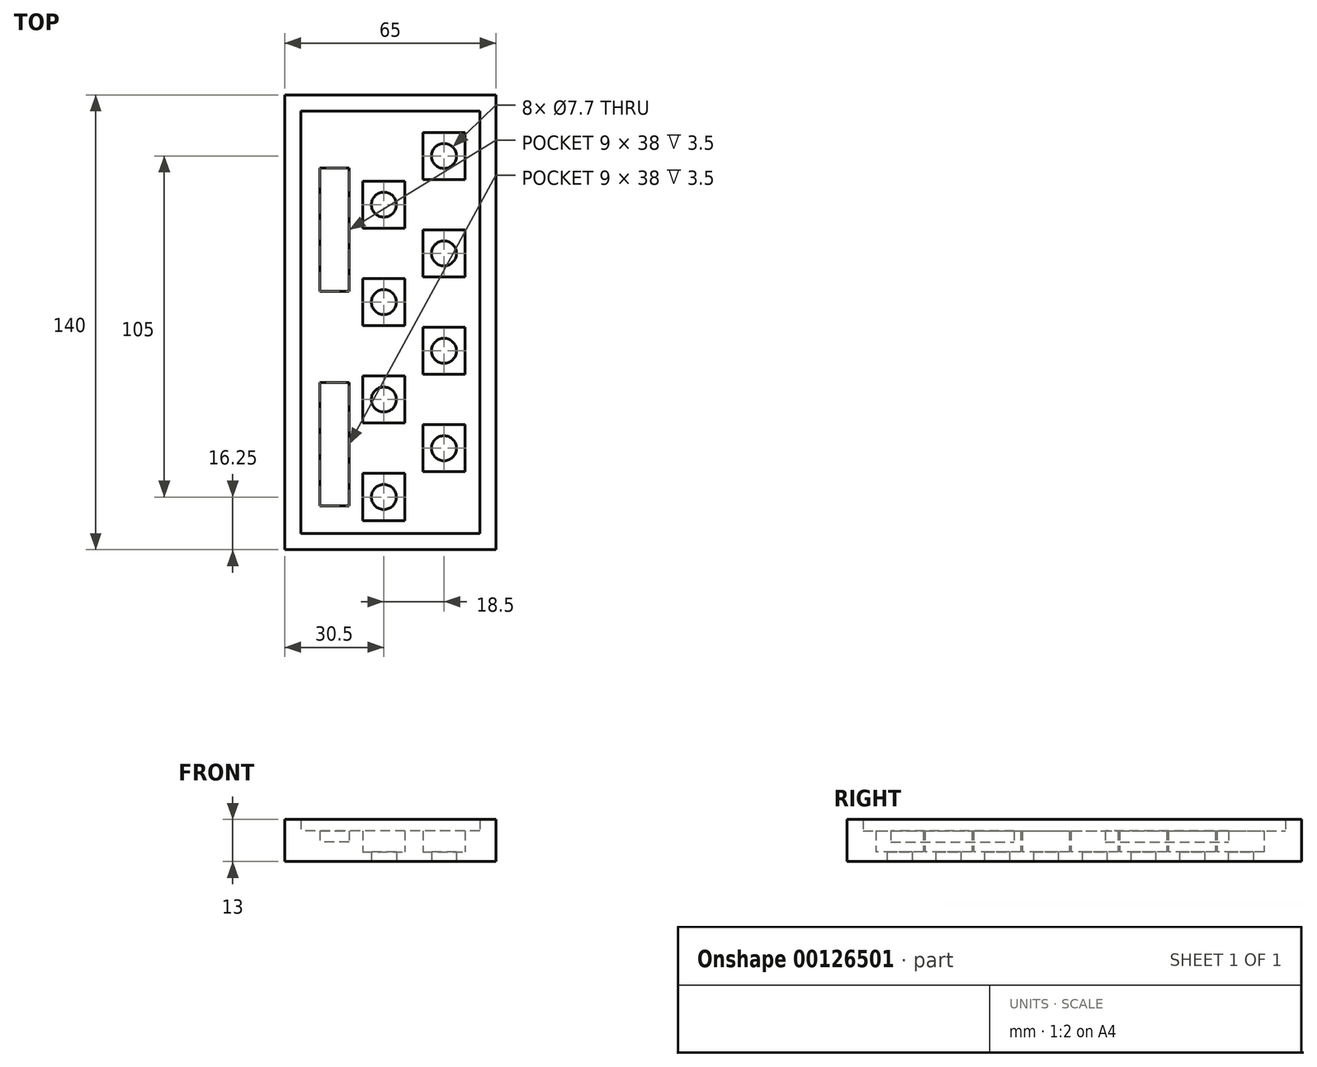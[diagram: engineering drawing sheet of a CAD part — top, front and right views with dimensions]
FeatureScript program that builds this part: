
annotation { "Feature Type Name" : "Feature", "Feature Type Description" : "" }
export const myFeature = defineFeature(function(context is Context, id is Id, definition is map)
    precondition{}
    {
        {
            var Q0;
            Q0=qCreatedBy(makeId("Top.planeOp"),FACE);
            var sketch = newSketch(context, id + "F0", { "sketchPlane" : qUnion([Q0])});
            skLineSegment(sketch, "E0.bottom", {"start": v(-63.75, 69.94) * mm, "end": v(1.25, 69.94) * mm});
            skLineSegment(sketch, "E0.top", {"start": v(-63.75, -70.06) * mm, "end": v(1.25, -70.06) * mm});
            skLineSegment(sketch, "E0.left", {"start": v(-63.75, 69.94) * mm, "end": v(-63.75, -70.06) * mm});
            skLineSegment(sketch, "E0.right", {"start": v(1.25, 69.94) * mm, "end": v(1.25, -70.06) * mm});
            skLineSegment(sketch, "E1.bottom", {"start": v(-8.25, 43.94) * mm, "end": v(-21.25, 43.94) * mm});
            skLineSegment(sketch, "E1.top", {"start": v(-8.25, 58.44) * mm, "end": v(-21.25, 58.44) * mm});
            skLineSegment(sketch, "E1.left", {"start": v(-8.25, 43.94) * mm, "end": v(-8.25, 58.44) * mm});
            skLineSegment(sketch, "E1.right", {"start": v(-21.25, 43.94) * mm, "end": v(-21.25, 58.44) * mm});
            skPoint(sketch, "E1.middle", {"position": v(-14.75, 51.2) * mm});
            skLineSegment(sketch, "E2.bottom", {"start": v(-26.75, 28.94) * mm, "end": v(-39.75, 28.94) * mm});
            skLineSegment(sketch, "E2.top", {"start": v(-26.75, 43.44) * mm, "end": v(-39.75, 43.44) * mm});
            skLineSegment(sketch, "E2.left", {"start": v(-26.75, 28.94) * mm, "end": v(-26.75, 43.44) * mm});
            skLineSegment(sketch, "E2.right", {"start": v(-39.75, 28.94) * mm, "end": v(-39.75, 43.44) * mm});
            skPoint(sketch, "E2.middle", {"position": v(-33.25, 36.2) * mm});
            skLineSegment(sketch, "E3.bottom", {"start": v(-8.25, 13.94) * mm, "end": v(-21.25, 13.94) * mm});
            skLineSegment(sketch, "E3.top", {"start": v(-8.25, 28.44) * mm, "end": v(-21.25, 28.44) * mm});
            skLineSegment(sketch, "E3.left", {"start": v(-8.25, 13.94) * mm, "end": v(-8.25, 28.44) * mm});
            skLineSegment(sketch, "E3.right", {"start": v(-21.25, 13.94) * mm, "end": v(-21.25, 28.44) * mm});
            skPoint(sketch, "E3.middle", {"position": v(-14.75, 21.2) * mm});
            skLineSegment(sketch, "E4.bottom", {"start": v(-26.75, -1.06) * mm, "end": v(-39.75, -1.06) * mm});
            skLineSegment(sketch, "E4.top", {"start": v(-26.75, 13.44) * mm, "end": v(-39.75, 13.44) * mm});
            skLineSegment(sketch, "E4.left", {"start": v(-26.75, -1.06) * mm, "end": v(-26.75, 13.44) * mm});
            skLineSegment(sketch, "E4.right", {"start": v(-39.75, -1.06) * mm, "end": v(-39.75, 13.44) * mm});
            skPoint(sketch, "E4.middle", {"position": v(-33.25, 6.2) * mm});
            skLineSegment(sketch, "E5.bottom", {"start": v(-8.25, -16.06) * mm, "end": v(-21.25, -16.06) * mm});
            skLineSegment(sketch, "E5.top", {"start": v(-8.25, -1.56) * mm, "end": v(-21.25, -1.56) * mm});
            skLineSegment(sketch, "E5.left", {"start": v(-8.25, -16.06) * mm, "end": v(-8.25, -1.56) * mm});
            skLineSegment(sketch, "E5.right", {"start": v(-21.25, -16.06) * mm, "end": v(-21.25, -1.56) * mm});
            skPoint(sketch, "E5.middle", {"position": v(-14.75, -8.8) * mm});
            skLineSegment(sketch, "E6.bottom", {"start": v(-26.75, -31.06) * mm, "end": v(-39.75, -31.06) * mm});
            skLineSegment(sketch, "E6.top", {"start": v(-26.75, -16.56) * mm, "end": v(-39.75, -16.56) * mm});
            skLineSegment(sketch, "E6.left", {"start": v(-26.75, -31.06) * mm, "end": v(-26.75, -16.56) * mm});
            skLineSegment(sketch, "E6.right", {"start": v(-39.75, -31.06) * mm, "end": v(-39.75, -16.56) * mm});
            skPoint(sketch, "E6.middle", {"position": v(-33.25, -23.8) * mm});
            skLineSegment(sketch, "E7.bottom", {"start": v(-8.25, -46.06) * mm, "end": v(-21.25, -46.06) * mm});
            skLineSegment(sketch, "E7.top", {"start": v(-8.25, -31.56) * mm, "end": v(-21.25, -31.56) * mm});
            skLineSegment(sketch, "E7.left", {"start": v(-8.25, -46.06) * mm, "end": v(-8.25, -31.56) * mm});
            skLineSegment(sketch, "E7.right", {"start": v(-21.25, -46.06) * mm, "end": v(-21.25, -31.56) * mm});
            skPoint(sketch, "E7.middle", {"position": v(-14.75, -38.8) * mm});
            skLineSegment(sketch, "E8.bottom", {"start": v(-26.75, -61.06) * mm, "end": v(-39.75, -61.06) * mm});
            skLineSegment(sketch, "E8.top", {"start": v(-26.75, -46.56) * mm, "end": v(-39.75, -46.56) * mm});
            skLineSegment(sketch, "E8.left", {"start": v(-26.75, -61.06) * mm, "end": v(-26.75, -46.56) * mm});
            skLineSegment(sketch, "E8.right", {"start": v(-39.75, -61.06) * mm, "end": v(-39.75, -46.56) * mm});
            skPoint(sketch, "E8.middle", {"position": v(-33.25, -53.8) * mm});
            skCircle(sketch, "E9", {"center": v(-14.75, 51.2) * mm, "radius": 3.85 * mm});
            skCircle(sketch, "E10", {"center": v(-33.25, 36.2) * mm, "radius": 3.85 * mm});
            skCircle(sketch, "E11", {"center": v(-14.75, 21.2) * mm, "radius": 3.85 * mm});
            skCircle(sketch, "E12", {"center": v(-33.25, 6.2) * mm, "radius": 3.85 * mm});
            skCircle(sketch, "E13", {"center": v(-14.75, -8.8) * mm, "radius": 3.85 * mm});
            skCircle(sketch, "E14", {"center": v(-33.25, -23.8) * mm, "radius": 3.85 * mm});
            skCircle(sketch, "E15", {"center": v(-14.75, -38.8) * mm, "radius": 3.85 * mm});
            skCircle(sketch, "E16", {"center": v(-33.25, -53.8) * mm, "radius": 3.85 * mm});
            skLineSegment(sketch, "E17", {"start": v(-26.75, -16.56) * mm, "end": v(1.25, -16.56) * mm, "construction": true});
            skLineSegment(sketch, "E18.bottom", {"start": v(-52.95, 47.44) * mm, "end": v(-43.95, 47.44) * mm, "construction": true});
            skLineSegment(sketch, "E18.top", {"start": v(-52.95, 9.44) * mm, "end": v(-43.95, 9.44) * mm, "construction": true});
            skLineSegment(sketch, "E18.left", {"start": v(-52.95, 47.44) * mm, "end": v(-52.95, 9.44) * mm, "construction": true});
            skLineSegment(sketch, "E18.right", {"start": v(-43.95, 47.44) * mm, "end": v(-43.95, 9.44) * mm, "construction": true});
            skLineSegment(sketch, "E19", {"start": v(-8.25, 58.44) * mm, "end": v(1.25, 58.44) * mm, "construction": true});
            skLineSegment(sketch, "E20", {"start": v(-39.75, -1.06) * mm, "end": v(-63.75, -1.06) * mm, "construction": true});
            skPoint(sketch, "E21.oppositeSnap0", {"position": v(-43.95, 28.44) * mm});
            skLineSegment(sketch, "E21.bottom", {"start": v(-52.95, -18.56) * mm, "end": v(-43.95, -18.56) * mm, "construction": true});
            skLineSegment(sketch, "E21.top", {"start": v(-52.95, -56.56) * mm, "end": v(-43.95, -56.56) * mm, "construction": true});
            skLineSegment(sketch, "E21.left", {"start": v(-52.95, -18.56) * mm, "end": v(-52.95, -56.56) * mm, "construction": true});
            skLineSegment(sketch, "E21.right", {"start": v(-43.95, -18.56) * mm, "end": v(-43.95, -56.56) * mm, "construction": true});
            skLineSegment(sketch, "E22", {"start": v(-26.75, -61.06) * mm, "end": v(-26.75, -70.06) * mm, "construction": true});
            skLineSegment(sketch, "E23", {"start": v(-8.25, -1.56) * mm, "end": v(1.25, -1.56) * mm, "construction": true});
            skLineSegment(sketch, "E24", {"start": v(1.25, 69.94) * mm, "end": v(1.25, 64.94) * mm, "construction": true});
            skLineSegment(sketch, "E25", {"start": v(1.25, 64.94) * mm, "end": v(-63.75, 64.94) * mm, "construction": true});
            skLineSegment(sketch, "E26", {"start": v(-63.75, 64.94) * mm, "end": v(-58.75, 64.94) * mm, "construction": true});
            skLineSegment(sketch, "E27", {"start": v(-58.75, 64.94) * mm, "end": v(-58.75, -70.06) * mm, "construction": true});
            skLineSegment(sketch, "E28", {"start": v(-58.75, -70.06) * mm, "end": v(-58.75, -65.06) * mm, "construction": true});
            skLineSegment(sketch, "E29", {"start": v(-26.75, -1.06) * mm, "end": v(1.25, -1.06) * mm, "construction": true});
            skLineSegment(sketch, "E30", {"start": v(-26.75, -31.06) * mm, "end": v(1.25, -31.06) * mm, "construction": true});
            skLineSegment(sketch, "E31", {"start": v(-26.75, -46.56) * mm, "end": v(1.25, -46.56) * mm, "construction": true});
            skLineSegment(sketch, "E32", {"start": v(-8.25, 58.44) * mm, "end": v(-8.25, 58.94) * mm, "construction": true});
            skLineSegment(sketch, "E33", {"start": v(-8.25, 58.94) * mm, "end": v(-58.75, 58.94) * mm, "construction": true});
            skLineSegment(sketch, "E34", {"start": v(-21.25, 64.94) * mm, "end": v(-21.25, 58.94) * mm, "construction": true});
            skLineSegment(sketch, "E35", {"start": v(1.25, 69.94) * mm, "end": v(-3.75, 69.94) * mm, "construction": true});
            skLineSegment(sketch, "E36", {"start": v(-3.75, 69.94) * mm, "end": v(-3.75, -70.06) * mm, "construction": true});
            skLineSegment(sketch, "E37", {"start": v(-8.25, 58.94) * mm, "end": v(-8.25, 64.94) * mm, "construction": true});
            skLineSegment(sketch, "E38", {"start": v(-8.25, 51.2) * mm, "end": v(1.25, 51.2) * mm, "construction": true});
            skLineSegment(sketch, "E39.bottom", {"start": v(-52.95, 47.44) * mm, "end": v(-43.95, 47.44) * mm});
            skLineSegment(sketch, "E39.top", {"start": v(-52.95, 9.44) * mm, "end": v(-43.95, 9.44) * mm});
            skLineSegment(sketch, "E39.left", {"start": v(-52.95, 47.44) * mm, "end": v(-52.95, 9.44) * mm});
            skLineSegment(sketch, "E39.right", {"start": v(-43.95, 47.44) * mm, "end": v(-43.95, 9.44) * mm});
            skLineSegment(sketch, "E40.bottom", {"start": v(-52.95, -18.56) * mm, "end": v(-43.95, -18.56) * mm});
            skLineSegment(sketch, "E40.top", {"start": v(-52.95, -56.56) * mm, "end": v(-43.95, -56.56) * mm});
            skLineSegment(sketch, "E40.left", {"start": v(-52.95, -18.56) * mm, "end": v(-52.95, -56.56) * mm});
            skLineSegment(sketch, "E40.right", {"start": v(-43.95, -18.56) * mm, "end": v(-43.95, -56.56) * mm});
            skLineSegment(sketch, "E41.bottom", {"start": v(-58.75, 64.94) * mm, "end": v(-3.75, 64.94) * mm});
            skLineSegment(sketch, "E41.top", {"start": v(-58.75, -65.06) * mm, "end": v(-3.75, -65.06) * mm});
            skLineSegment(sketch, "E41.left", {"start": v(-58.75, 64.94) * mm, "end": v(-58.75, -65.06) * mm});
            skLineSegment(sketch, "E41.right", {"start": v(-3.75, 64.94) * mm, "end": v(-3.75, -65.06) * mm});
            skLineSegment(sketch, "E42", {"start": v(-26.75, 64.94) * mm, "end": v(-26.75, -65.06) * mm, "construction": true});
            skLineSegment(sketch, "E43", {"start": v(-8.25, 43.94) * mm, "end": v(1.25, 43.94) * mm, "construction": true});
            skLineSegment(sketch, "E44", {"start": v(-26.75, 43.44) * mm, "end": v(1.25, 43.44) * mm, "construction": true});
            skLineSegment(sketch, "E45", {"start": v(-26.75, 28.94) * mm, "end": v(1.25, 28.94) * mm, "construction": true});
            skLineSegment(sketch, "E46", {"start": v(-8.25, 28.44) * mm, "end": v(1.25, 28.44) * mm, "construction": true});
            skLineSegment(sketch, "E47", {"start": v(-8.25, 13.94) * mm, "end": v(1.25, 13.94) * mm, "construction": true});
            skLineSegment(sketch, "E48", {"start": v(-26.75, 13.44) * mm, "end": v(1.25, 13.44) * mm, "construction": true});
            skLineSegment(sketch, "E49", {"start": v(-3.75, -61.06) * mm, "end": v(-3.75, -65.06) * mm, "construction": true});
            skLineSegment(sketch, "E50", {"start": v(-3.75, 64.94) * mm, "end": v(-3.75, 60.57) * mm, "construction": true});
            skLineSegment(sketch, "E51", {"start": v(-3.75, 64.94) * mm, "end": v(-3.75, 64.44) * mm, "construction": true});
            skLineSegment(sketch, "E52", {"start": v(-3.75, 64.44) * mm, "end": v(-3.75, 60.44) * mm, "construction": true});
            skLineSegment(sketch, "E53.left", {"start": v(-3.75, 60.44) * mm, "end": v(-3.75, 49.54) * mm});
            skSolve(sketch);
        }
        {
            var Q0;
            Q0=makeQuery(id+"F0.imprint","IMPRINT",FACE,{"disambiguationData":[TD([[makeQuery(id+"F0.imprint","IMPRINT",EDGE,{"derivedFrom":sQuery(id+"F0.wireOp",EDGE,"E0.bottom")}),-1.0]])]});
            var Q1;
            Q1=makeQuery(id+"F0.imprint","IMPRINT",FACE,{"disambiguationData":[TD([[makeQuery(id+"F0.imprint","IMPRINT",EDGE,{"derivedFrom":sQuery(id+"F0.wireOp",EDGE,"E39.bottom")}),-1.0]])]});
            var Q2;
            Q2=makeQuery(id+"F0.imprint","IMPRINT",FACE,{"disambiguationData":[TD([[makeQuery(id+"F0.imprint","IMPRINT",EDGE,{"derivedFrom":sQuery(id+"F0.wireOp",EDGE,"E40.bottom")}),-1.0]])]});
            var Q3;
            Q3=makeQuery(id+"F0.imprint","IMPRINT",FACE,{"disambiguationData":[TD([[makeQuery(id+"F0.imprint","IMPRINT",EDGE,{"derivedFrom":sQuery(id+"F0.wireOp",EDGE,"E1.bottom")}),-1.0]])]});
            var Q4;
            Q4=makeQuery(id+"F0.imprint","IMPRINT",FACE,{"disambiguationData":[TD([[makeQuery(id+"F0.imprint","IMPRINT",EDGE,{"derivedFrom":sQuery(id+"F0.wireOp",EDGE,"E2.bottom")}),-1.0]])]});
            var Q5;
            Q5=makeQuery(id+"F0.imprint","IMPRINT",FACE,{"disambiguationData":[TD([[makeQuery(id+"F0.imprint","IMPRINT",EDGE,{"derivedFrom":sQuery(id+"F0.wireOp",EDGE,"E3.bottom")}),-1.0]])]});
            var Q6;
            Q6=makeQuery(id+"F0.imprint","IMPRINT",FACE,{"disambiguationData":[TD([[makeQuery(id+"F0.imprint","IMPRINT",EDGE,{"derivedFrom":sQuery(id+"F0.wireOp",EDGE,"E4.bottom")}),-1.0]])]});
            var Q7;
            Q7=makeQuery(id+"F0.imprint","IMPRINT",FACE,{"disambiguationData":[TD([[makeQuery(id+"F0.imprint","IMPRINT",EDGE,{"derivedFrom":sQuery(id+"F0.wireOp",EDGE,"E5.bottom")}),-1.0]])]});
            var Q8;
            Q8=makeQuery(id+"F0.imprint","IMPRINT",FACE,{"disambiguationData":[TD([[makeQuery(id+"F0.imprint","IMPRINT",EDGE,{"derivedFrom":sQuery(id+"F0.wireOp",EDGE,"E6.bottom")}),-1.0]])]});
            var Q9;
            Q9=makeQuery(id+"F0.imprint","IMPRINT",FACE,{"disambiguationData":[TD([[makeQuery(id+"F0.imprint","IMPRINT",EDGE,{"derivedFrom":sQuery(id+"F0.wireOp",EDGE,"E8.bottom")}),-1.0]])]});
            var Q10;
            Q10=makeQuery(id+"F0.imprint","IMPRINT",FACE,{"disambiguationData":[TD([[makeQuery(id+"F0.imprint","IMPRINT",EDGE,{"derivedFrom":sQuery(id+"F0.wireOp",EDGE,"E7.bottom")}),-1.0]])]});
            var Q11;
            Q11=makeQuery(id+"F0.imprint","IMPRINT",FACE,{"disambiguationData":[TD([[makeQuery(id+"F0.imprint","IMPRINT",EDGE,{"derivedFrom":sQuery(id+"F0.wireOp",EDGE,"E1.bottom")}),1.0]])]});
            extrude(context, id + "F1", {"entities" : qUnion([Q0, Q1, Q2, Q3, Q4, Q5, Q6, Q7, Q8, Q9, Q10, Q11]), "depth" : 3 * mm});
        }
        {
            var Q0;
            Q0=makeQuery(id+"F0.imprint","IMPRINT",FACE,{"disambiguationData":[TD([[makeQuery(id+"F0.imprint","IMPRINT",EDGE,{"derivedFrom":sQuery(id+"F0.wireOp",EDGE,"E1.bottom")}),1.0]])]});
            var Q1;
            Q1=makeQuery(id+"F0.imprint","IMPRINT",FACE,{"disambiguationData":[TD([[makeQuery(id+"F0.imprint","IMPRINT",EDGE,{"derivedFrom":sQuery(id+"F0.wireOp",EDGE,"E0.bottom")}),-1.0]])]});
            var Q2;
            Q2=makeQuery(id+"F0.imprint","IMPRINT",FACE,{"disambiguationData":[TD([[makeQuery(id+"F0.imprint","IMPRINT",EDGE,{"derivedFrom":sQuery(id+"F0.wireOp",EDGE,"E39.bottom")}),-1.0]])]});
            var Q3;
            Q3=makeQuery(id+"F0.imprint","IMPRINT",FACE,{"disambiguationData":[TD([[makeQuery(id+"F0.imprint","IMPRINT",EDGE,{"derivedFrom":sQuery(id+"F0.wireOp",EDGE,"E40.bottom")}),-1.0]])]});
            extrude(context, id + "F2", {"entities" : qUnion([Q0, Q1, Q2, Q3]), "operationType" : NewBodyOperationType.ADD, "depth" : 6 * mm});
        }
        {
            var Q0;
            Q0=makeQuery(id+"F0.imprint","IMPRINT",FACE,{"disambiguationData":[TD([[makeQuery(id+"F0.imprint","IMPRINT",EDGE,{"derivedFrom":sQuery(id+"F0.wireOp",EDGE,"E1.bottom")}),1.0]])]});
            var Q1;
            Q1=makeQuery(id+"F0.imprint","IMPRINT",FACE,{"disambiguationData":[TD([[makeQuery(id+"F0.imprint","IMPRINT",EDGE,{"derivedFrom":sQuery(id+"F0.wireOp",EDGE,"E0.bottom")}),-1.0]])]});
            var Q2;
            Q2=makeQuery(id+"F0.imprint","IMPRINT",FACE,{"disambiguationData":[TD([[makeQuery(id+"F0.imprint","IMPRINT",EDGE,{"derivedFrom":sQuery(id+"F0.wireOp",EDGE,"E53.bottom")}),-1.0]])]});
            extrude(context, id + "F3", {"entities" : qUnion([Q0, Q1, Q2]), "operationType" : NewBodyOperationType.ADD, "depth" : 9.5 * mm});
        }
        {
            var Q0;
            Q0=makeQuery(id+"F0.imprint","IMPRINT",FACE,{"disambiguationData":[TD([[makeQuery(id+"F0.imprint","IMPRINT",EDGE,{"derivedFrom":sQuery(id+"F0.wireOp",EDGE,"E0.bottom")}),-1.0]])]});
            extrude(context, id + "F4", {"entities" : qUnion([Q0]), "operationType" : NewBodyOperationType.ADD, "depth" : 13 * mm});
        }
    });
